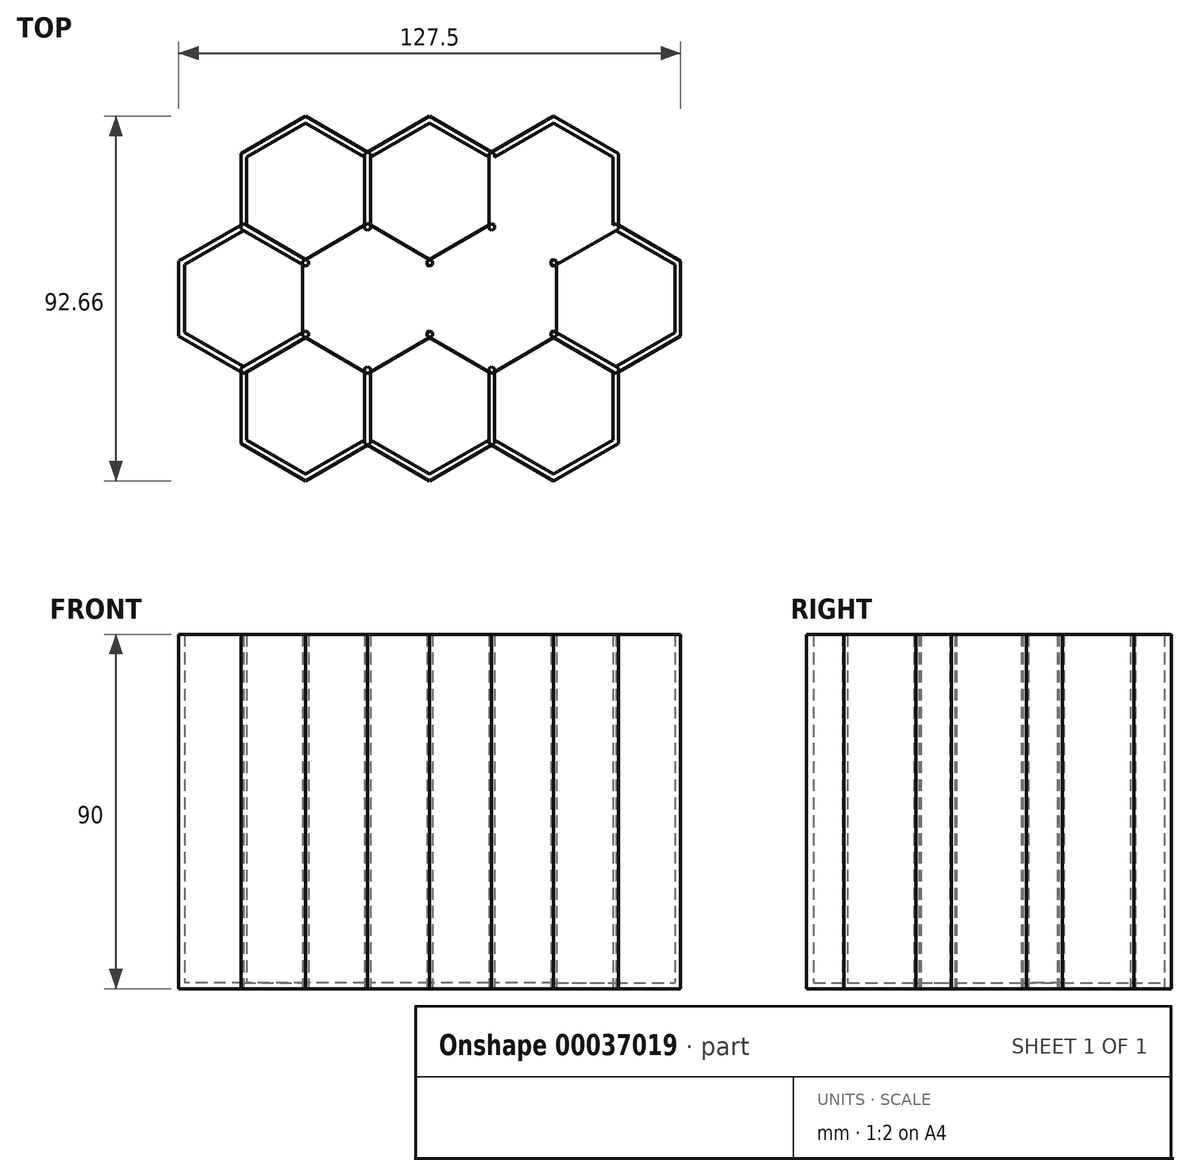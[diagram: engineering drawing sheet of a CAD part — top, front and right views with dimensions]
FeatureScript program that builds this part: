
annotation { "Feature Type Name" : "Feature", "Feature Type Description" : "" }
export const myFeature = defineFeature(function(context is Context, id is Id, definition is map)
    precondition{}
    {
        {
            assignVariable(context, id + "F0", {"name" : "WallThickness", "anyValue" : 1.5});
        }
        {
            var Q0;
            Q0=qCreatedBy(makeId("Top.planeOp"),FACE);
            var sketch = newSketch(context, id + "F1", { "sketchPlane" : qUnion([Q0])});
            skCircle(sketch, "E0.cCircle", {"center": v(0, 0) * mm, "radius": 15 * mm, "construction": true});
            skLineSegment(sketch, "E0.0", {"start": v(0, 17.32) * mm, "end": v(15, 8.66) * mm});
            skLineSegment(sketch, "E0.1", {"start": v(15, 8.66) * mm, "end": v(15, -8.66) * mm});
            skLineSegment(sketch, "E0.2", {"start": v(15, -8.66) * mm, "end": v(0, -17.32) * mm});
            skLineSegment(sketch, "E0.3", {"start": v(0, -17.32) * mm, "end": v(-15, -8.66) * mm});
            skLineSegment(sketch, "E0.4", {"start": v(-15, -8.66) * mm, "end": v(-15, 8.66) * mm});
            skLineSegment(sketch, "E0.5", {"start": v(-15, 8.66) * mm, "end": v(0, 17.32) * mm});
            skPoint(sketch, "E0.0.midPoint", {"position": v(7.5, 13) * mm});
            skLineSegment(sketch, "E1.0", {"start": v(-16.5, 9.53) * mm, "end": v(0, 19.05) * mm});
            skLineSegment(sketch, "E1.1", {"start": v(-16.5, -9.53) * mm, "end": v(-16.5, 9.53) * mm});
            skLineSegment(sketch, "E1.2", {"start": v(0, -19.05) * mm, "end": v(-16.5, -9.53) * mm});
            skLineSegment(sketch, "E1.3", {"start": v(16.5, -9.53) * mm, "end": v(0, -19.05) * mm});
            skLineSegment(sketch, "E1.4", {"start": v(16.5, 9.53) * mm, "end": v(16.5, -9.53) * mm});
            skLineSegment(sketch, "E1.5", {"start": v(0, 19.05) * mm, "end": v(16.5, 9.53) * mm});
            skCircle(sketch, "E2.1.0.0", {"center": v(31.5, 0) * mm, "radius": 15 * mm, "construction": true});
            skLineSegment(sketch, "E2.1.0.1", {"start": v(46.5, 8.66) * mm, "end": v(46.5, -8.66) * mm});
            skLineSegment(sketch, "E2.1.0.2", {"start": v(46.5, -8.66) * mm, "end": v(31.5, -17.32) * mm});
            skPoint(sketch, "E2.1.0.3", {"position": v(39, 13) * mm});
            skLineSegment(sketch, "E2.1.0.4", {"start": v(31.5, -19.05) * mm, "end": v(15, -9.53) * mm});
            skLineSegment(sketch, "E2.1.0.5", {"start": v(31.5, -17.32) * mm, "end": v(16.5, -8.66) * mm});
            skLineSegment(sketch, "E2.1.0.6", {"start": v(16.5, -8.66) * mm, "end": v(16.5, 8.66) * mm});
            skLineSegment(sketch, "E2.1.0.7", {"start": v(15, 9.53) * mm, "end": v(31.5, 19.05) * mm});
            skLineSegment(sketch, "E2.1.0.8", {"start": v(15, -9.53) * mm, "end": v(15, 9.53) * mm});
            skLineSegment(sketch, "E2.1.0.9", {"start": v(48, -9.53) * mm, "end": v(31.5, -19.05) * mm});
            skLineSegment(sketch, "E2.1.0.10", {"start": v(48, 9.53) * mm, "end": v(48, -9.53) * mm});
            skLineSegment(sketch, "E2.1.0.11", {"start": v(31.5, 19.05) * mm, "end": v(48, 9.53) * mm});
            skLineSegment(sketch, "E2.1.0.12", {"start": v(31.5, 17.32) * mm, "end": v(46.5, 8.66) * mm});
            skLineSegment(sketch, "E2.1.0.13", {"start": v(16.5, 8.66) * mm, "end": v(31.5, 17.32) * mm});
            skCircle(sketch, "E2.2.0.0", {"center": v(63, 0) * mm, "radius": 15 * mm, "construction": true});
            skLineSegment(sketch, "E2.2.0.1", {"start": v(78, 8.66) * mm, "end": v(78, -8.66) * mm});
            skLineSegment(sketch, "E2.2.0.2", {"start": v(78, -8.66) * mm, "end": v(63, -17.32) * mm});
            skPoint(sketch, "E2.2.0.3", {"position": v(70.5, 13) * mm});
            skLineSegment(sketch, "E2.2.0.4", {"start": v(63, -19.05) * mm, "end": v(46.5, -9.53) * mm});
            skLineSegment(sketch, "E2.2.0.5", {"start": v(63, -17.32) * mm, "end": v(48, -8.66) * mm});
            skLineSegment(sketch, "E2.2.0.6", {"start": v(48, -8.66) * mm, "end": v(48, 8.66) * mm});
            skLineSegment(sketch, "E2.2.0.7", {"start": v(46.5, 9.53) * mm, "end": v(63, 19.05) * mm});
            skLineSegment(sketch, "E2.2.0.8", {"start": v(46.5, -9.53) * mm, "end": v(46.5, 9.53) * mm});
            skLineSegment(sketch, "E2.2.0.9", {"start": v(79.5, -9.53) * mm, "end": v(63, -19.05) * mm});
            skLineSegment(sketch, "E2.2.0.10", {"start": v(79.5, 9.53) * mm, "end": v(79.5, -9.53) * mm});
            skLineSegment(sketch, "E2.2.0.11", {"start": v(63, 19.05) * mm, "end": v(79.5, 9.53) * mm});
            skLineSegment(sketch, "E2.2.0.12", {"start": v(63, 17.32) * mm, "end": v(78, 8.66) * mm});
            skLineSegment(sketch, "E2.2.0.13", {"start": v(48, 8.66) * mm, "end": v(63, 17.32) * mm});
            skLineSegment(sketch, "E2.direction1", {"start": v(0, 0) * mm, "end": v(31.5, 0) * mm, "construction": true});
            skLineSegment(sketch, "E3.1.0.0", {"start": v(-15.75, 46.33) * mm, "end": v(0.75, 36.8) * mm});
            skLineSegment(sketch, "E3.1.0.1", {"start": v(-15.75, 27.28) * mm, "end": v(15.75, 27.28) * mm, "construction": true});
            skLineSegment(sketch, "E3.1.0.2", {"start": v(-30.75, 18.62) * mm, "end": v(-30.75, 35.94) * mm});
            skLineSegment(sketch, "E3.1.0.3", {"start": v(-15.75, 9.96) * mm, "end": v(-30.75, 18.62) * mm});
            skLineSegment(sketch, "E3.1.0.4", {"start": v(-0.75, 18.62) * mm, "end": v(-15.75, 9.96) * mm});
            skLineSegment(sketch, "E3.1.0.5", {"start": v(-0.75, 35.94) * mm, "end": v(-0.75, 18.62) * mm});
            skLineSegment(sketch, "E3.1.0.6", {"start": v(0.75, 36.8) * mm, "end": v(0.75, 17.75) * mm});
            skPoint(sketch, "E3.1.0.7", {"position": v(-8.25, 40.27) * mm});
            skLineSegment(sketch, "E3.1.0.8", {"start": v(-15.75, 44.6) * mm, "end": v(-0.75, 35.94) * mm});
            skCircle(sketch, "E3.1.0.9", {"center": v(-15.75, 27.28) * mm, "radius": 15 * mm, "construction": true});
            skLineSegment(sketch, "E3.1.0.10", {"start": v(-32.25, 17.75) * mm, "end": v(-32.25, 36.8) * mm});
            skLineSegment(sketch, "E3.1.0.11", {"start": v(-15.75, 8.23) * mm, "end": v(-32.25, 17.75) * mm});
            skLineSegment(sketch, "E3.1.0.12", {"start": v(0.75, 17.75) * mm, "end": v(-15.75, 8.23) * mm});
            skLineSegment(sketch, "E3.1.0.13", {"start": v(-30.75, 35.94) * mm, "end": v(-15.75, 44.6) * mm});
            skLineSegment(sketch, "E3.1.0.14", {"start": v(-32.25, 36.8) * mm, "end": v(-15.75, 46.33) * mm});
            skLineSegment(sketch, "E3.direction1", {"start": v(0, 0) * mm, "end": v(-15.75, 27.28) * mm, "construction": true});
            skLineSegment(sketch, "E4.1.0.0", {"start": v(0.75, 35.94) * mm, "end": v(15.75, 44.6) * mm});
            skLineSegment(sketch, "E4.1.0.1", {"start": v(30.75, 35.94) * mm, "end": v(30.75, 18.62) * mm});
            skLineSegment(sketch, "E4.1.0.2", {"start": v(15.75, 8.23) * mm, "end": v(-0.75, 17.75) * mm});
            skLineSegment(sketch, "E4.1.0.3", {"start": v(0.75, 18.62) * mm, "end": v(0.75, 35.94) * mm});
            skLineSegment(sketch, "E4.1.0.4", {"start": v(32.25, 36.8) * mm, "end": v(32.25, 17.75) * mm});
            skLineSegment(sketch, "E4.1.0.5", {"start": v(-0.75, 36.8) * mm, "end": v(15.75, 46.33) * mm});
            skPoint(sketch, "E4.1.0.6", {"position": v(23.25, 40.27) * mm});
            skLineSegment(sketch, "E4.1.0.7", {"start": v(32.25, 17.75) * mm, "end": v(15.75, 8.23) * mm});
            skCircle(sketch, "E4.1.0.8", {"center": v(15.75, 27.28) * mm, "radius": 15 * mm, "construction": true});
            skLineSegment(sketch, "E4.1.0.9", {"start": v(-0.75, 17.75) * mm, "end": v(-0.75, 36.8) * mm});
            skLineSegment(sketch, "E4.1.0.10", {"start": v(30.75, 18.62) * mm, "end": v(15.75, 9.96) * mm});
            skLineSegment(sketch, "E4.1.0.11", {"start": v(15.75, 46.33) * mm, "end": v(32.25, 36.8) * mm});
            skLineSegment(sketch, "E4.1.0.12", {"start": v(15.75, 9.96) * mm, "end": v(0.75, 18.62) * mm});
            skLineSegment(sketch, "E4.1.0.13", {"start": v(15.75, 44.6) * mm, "end": v(30.75, 35.94) * mm});
            skLineSegment(sketch, "E4.2.0.0", {"start": v(32.25, 35.94) * mm, "end": v(47.25, 44.6) * mm});
            skLineSegment(sketch, "E4.2.0.1", {"start": v(62.25, 35.94) * mm, "end": v(62.25, 18.62) * mm});
            skLineSegment(sketch, "E4.2.0.2", {"start": v(47.25, 8.23) * mm, "end": v(30.75, 17.75) * mm});
            skLineSegment(sketch, "E4.2.0.3", {"start": v(32.25, 18.62) * mm, "end": v(32.25, 35.94) * mm});
            skLineSegment(sketch, "E4.2.0.4", {"start": v(63.75, 36.8) * mm, "end": v(63.75, 17.75) * mm});
            skLineSegment(sketch, "E4.2.0.5", {"start": v(30.75, 36.8) * mm, "end": v(47.25, 46.33) * mm});
            skPoint(sketch, "E4.2.0.6", {"position": v(54.75, 40.27) * mm});
            skLineSegment(sketch, "E4.2.0.7", {"start": v(63.75, 17.75) * mm, "end": v(47.25, 8.23) * mm});
            skCircle(sketch, "E4.2.0.8", {"center": v(47.25, 27.28) * mm, "radius": 15 * mm, "construction": true});
            skLineSegment(sketch, "E4.2.0.9", {"start": v(30.75, 17.75) * mm, "end": v(30.75, 36.8) * mm});
            skLineSegment(sketch, "E4.2.0.10", {"start": v(62.25, 18.62) * mm, "end": v(47.25, 9.96) * mm});
            skLineSegment(sketch, "E4.2.0.11", {"start": v(47.25, 46.33) * mm, "end": v(63.75, 36.8) * mm});
            skLineSegment(sketch, "E4.2.0.12", {"start": v(47.25, 9.96) * mm, "end": v(32.25, 18.62) * mm});
            skLineSegment(sketch, "E4.2.0.13", {"start": v(47.25, 44.6) * mm, "end": v(62.25, 35.94) * mm});
            skLineSegment(sketch, "E4.3.0.0", {"start": v(63.75, 35.94) * mm, "end": v(78.75, 44.6) * mm});
            skLineSegment(sketch, "E4.3.0.1", {"start": v(93.75, 35.94) * mm, "end": v(93.75, 18.62) * mm});
            skLineSegment(sketch, "E4.3.0.2", {"start": v(78.75, 8.23) * mm, "end": v(62.25, 17.75) * mm});
            skLineSegment(sketch, "E4.3.0.3", {"start": v(63.75, 18.62) * mm, "end": v(63.75, 35.94) * mm});
            skLineSegment(sketch, "E4.3.0.4", {"start": v(95.25, 36.8) * mm, "end": v(95.25, 17.75) * mm});
            skLineSegment(sketch, "E4.3.0.5", {"start": v(62.25, 36.8) * mm, "end": v(78.75, 46.33) * mm});
            skPoint(sketch, "E4.3.0.6", {"position": v(86.25, 40.27) * mm});
            skLineSegment(sketch, "E4.3.0.7", {"start": v(95.25, 17.75) * mm, "end": v(78.75, 8.23) * mm});
            skCircle(sketch, "E4.3.0.8", {"center": v(78.75, 27.28) * mm, "radius": 15 * mm, "construction": true});
            skLineSegment(sketch, "E4.3.0.9", {"start": v(62.25, 17.75) * mm, "end": v(62.25, 36.8) * mm});
            skLineSegment(sketch, "E4.3.0.10", {"start": v(93.75, 18.62) * mm, "end": v(78.75, 9.96) * mm});
            skLineSegment(sketch, "E4.3.0.11", {"start": v(78.75, 46.33) * mm, "end": v(95.25, 36.8) * mm});
            skLineSegment(sketch, "E4.3.0.12", {"start": v(78.75, 9.96) * mm, "end": v(63.75, 18.62) * mm});
            skLineSegment(sketch, "E4.3.0.13", {"start": v(78.75, 44.6) * mm, "end": v(93.75, 35.94) * mm});
            skLineSegment(sketch, "E5.1.0.0", {"start": v(-15, 45.9) * mm, "end": v(-15, 63.22) * mm});
            skLineSegment(sketch, "E5.1.0.1", {"start": v(78, 45.9) * mm, "end": v(63, 37.24) * mm});
            skLineSegment(sketch, "E5.1.0.2", {"start": v(0, 37.24) * mm, "end": v(-15, 45.9) * mm});
            skLineSegment(sketch, "E5.1.0.3", {"start": v(48, 64.09) * mm, "end": v(48, 45.03) * mm});
            skLineSegment(sketch, "E5.1.0.4", {"start": v(79.5, 45.03) * mm, "end": v(63, 35.5) * mm});
            skLineSegment(sketch, "E5.1.0.5", {"start": v(79.5, 64.09) * mm, "end": v(79.5, 45.03) * mm});
            skPoint(sketch, "E5.1.0.6", {"position": v(7.5, 67.55) * mm});
            skLineSegment(sketch, "E5.1.0.7", {"start": v(-15, 63.22) * mm, "end": v(0, 71.88) * mm});
            skLineSegment(sketch, "E5.1.0.8", {"start": v(0, 73.61) * mm, "end": v(16.5, 64.09) * mm});
            skLineSegment(sketch, "E5.1.0.9", {"start": v(15, 63.22) * mm, "end": v(15, 45.9) * mm});
            skLineSegment(sketch, "E5.1.0.10", {"start": v(48, 45.03) * mm, "end": v(31.5, 35.5) * mm});
            skLineSegment(sketch, "E5.1.0.11", {"start": v(48, 45.9) * mm, "end": v(48, 63.22) * mm});
            skLineSegment(sketch, "E5.1.0.12", {"start": v(46.5, 63.22) * mm, "end": v(46.5, 45.9) * mm});
            skCircle(sketch, "E5.1.0.13", {"center": v(63, 54.56) * mm, "radius": 15 * mm, "construction": true});
            skLineSegment(sketch, "E5.1.0.14", {"start": v(16.5, 63.22) * mm, "end": v(31.5, 71.88) * mm});
            skLineSegment(sketch, "E5.1.0.15", {"start": v(0, 71.88) * mm, "end": v(15, 63.22) * mm});
            skPoint(sketch, "E5.1.0.16", {"position": v(39, 67.55) * mm});
            skLineSegment(sketch, "E5.1.0.17", {"start": v(63, 35.5) * mm, "end": v(46.5, 45.03) * mm});
            skLineSegment(sketch, "E5.1.0.18", {"start": v(63, 37.24) * mm, "end": v(48, 45.9) * mm});
            skLineSegment(sketch, "E5.1.0.19", {"start": v(15, 45.03) * mm, "end": v(15, 64.09) * mm});
            skLineSegment(sketch, "E5.1.0.20", {"start": v(15, 64.09) * mm, "end": v(31.5, 73.61) * mm});
            skLineSegment(sketch, "E5.1.0.21", {"start": v(31.5, 73.61) * mm, "end": v(48, 64.09) * mm});
            skLineSegment(sketch, "E5.1.0.22", {"start": v(-16.5, 45.03) * mm, "end": v(-16.5, 64.09) * mm});
            skLineSegment(sketch, "E5.1.0.23", {"start": v(46.5, 45.03) * mm, "end": v(46.5, 64.09) * mm});
            skLineSegment(sketch, "E5.1.0.24", {"start": v(63, 73.61) * mm, "end": v(79.5, 64.09) * mm});
            skLineSegment(sketch, "E5.1.0.25", {"start": v(48, 63.22) * mm, "end": v(63, 71.88) * mm});
            skLineSegment(sketch, "E5.1.0.26", {"start": v(31.5, 35.5) * mm, "end": v(15, 45.03) * mm});
            skCircle(sketch, "E5.1.0.27", {"center": v(0, 54.56) * mm, "radius": 15 * mm, "construction": true});
            skLineSegment(sketch, "E5.1.0.28", {"start": v(0, 54.56) * mm, "end": v(31.5, 54.56) * mm, "construction": true});
            skLineSegment(sketch, "E5.1.0.29", {"start": v(46.5, 64.09) * mm, "end": v(63, 73.61) * mm});
            skLineSegment(sketch, "E5.1.0.30", {"start": v(31.5, 37.24) * mm, "end": v(16.5, 45.9) * mm});
            skLineSegment(sketch, "E5.1.0.31", {"start": v(0, 35.5) * mm, "end": v(-16.5, 45.03) * mm});
            skLineSegment(sketch, "E5.1.0.32", {"start": v(15, 45.9) * mm, "end": v(0, 37.24) * mm});
            skCircle(sketch, "E5.1.0.33", {"center": v(31.5, 54.56) * mm, "radius": 15 * mm, "construction": true});
            skLineSegment(sketch, "E5.1.0.34", {"start": v(78, 63.22) * mm, "end": v(78, 45.9) * mm});
            skLineSegment(sketch, "E5.1.0.35", {"start": v(16.5, 64.09) * mm, "end": v(16.5, 45.03) * mm});
            skLineSegment(sketch, "E5.1.0.36", {"start": v(16.5, 45.03) * mm, "end": v(0, 35.5) * mm});
            skLineSegment(sketch, "E5.1.0.37", {"start": v(-16.5, 64.09) * mm, "end": v(0, 73.61) * mm});
            skLineSegment(sketch, "E5.1.0.38", {"start": v(16.5, 45.9) * mm, "end": v(16.5, 63.22) * mm});
            skLineSegment(sketch, "E5.1.0.39", {"start": v(46.5, 45.9) * mm, "end": v(31.5, 37.24) * mm});
            skLineSegment(sketch, "E5.1.0.40", {"start": v(0, 54.56) * mm, "end": v(31.5, 54.56) * mm, "construction": true});
            skPoint(sketch, "E5.1.0.41", {"position": v(70.5, 67.55) * mm});
            skLineSegment(sketch, "E5.1.0.42", {"start": v(31.5, 71.88) * mm, "end": v(46.5, 63.22) * mm});
            skLineSegment(sketch, "E5.1.0.43", {"start": v(63, 71.88) * mm, "end": v(78, 63.22) * mm});
            skLineSegment(sketch, "E5.direction1", {"start": v(-15.75, 27.28) * mm, "end": v(0, 54.56) * mm, "construction": true});
            skSolve(sketch);
        }
        {
            assignVariable(context, id + "F2", {"name" : "Height", "anyValue" : 90});
        }
        {
            var Q0;
            {var subQ2=sQuery(id+"F1.wireOp",EDGE,"E5.1.0.14");Q0=makeQuery(id+"F1.imprint","IMPRINT",FACE,{"disambiguationData":[TD([[makeQuery(id+"F1.imprint","IMPRINT",EDGE,{"derivedFrom":subQ2}),1.0]])]});}
            var Q1;
            {var subQ10=sQuery(id+"F1.wireOp",EDGE,"E5.1.0.0");Q1=makeQuery(id+"F1.imprint","IMPRINT",FACE,{"disambiguationData":[TD([[makeQuery(id+"F1.imprint","IMPRINT",EDGE,{"derivedFrom":subQ10}),1.0]])]});}
            var Q2;
            Q2=makeQuery(id+"F1.imprint","IMPRINT",FACE,{"disambiguationData":[TD([[makeQuery(id+"F1.imprint","IMPRINT",EDGE,{"derivedFrom":sQuery(id+"F1.wireOp",EDGE,"E4.3.0.1")}),1.0]])]});
            var Q3;
            {var subQ5=sQuery(id+"F1.wireOp",EDGE,"E2.2.0.1");Q3=makeQuery(id+"F1.imprint","IMPRINT",FACE,{"disambiguationData":[TD([[makeQuery(id+"F1.imprint","IMPRINT",EDGE,{"derivedFrom":subQ5}),1.0]])]});}
            var Q4;
            {var subQ3=sQuery(id+"F1.wireOp",EDGE,"E2.1.0.2");Q4=makeQuery(id+"F1.imprint","IMPRINT",FACE,{"disambiguationData":[TD([[makeQuery(id+"F1.imprint","IMPRINT",EDGE,{"derivedFrom":subQ3}),1.0]])]});}
            var Q5;
            Q5=makeQuery(id+"F1.imprint","IMPRINT",FACE,{"disambiguationData":[TD([[makeQuery(id+"F1.imprint","IMPRINT",EDGE,{"derivedFrom":sQuery(id+"F1.wireOp",EDGE,"E3.1.0.2")}),1.0]])]});
            var Q6;
            {var subQ9=sQuery(id+"F1.wireOp",EDGE,"E0.2");Q6=makeQuery(id+"F1.imprint","IMPRINT",FACE,{"disambiguationData":[TD([[makeQuery(id+"F1.imprint","IMPRINT",EDGE,{"derivedFrom":subQ9}),1.0]])]});}
            var Q7;
            {var subQ4=sQuery(id+"F1.wireOp",EDGE,"E2.1.0.6");Q7=makeQuery(id+"F1.imprint","IMPRINT",FACE,{"disambiguationData":[TD([[makeQuery(id+"F1.imprint","IMPRINT",EDGE,{"derivedFrom":subQ4}),1.0]])]});}
            var Q8;
            {var subQ4=sQuery(id+"F1.wireOp",EDGE,"E5.1.0.24");Q8=makeQuery(id+"F1.imprint","IMPRINT",FACE,{"disambiguationData":[TD([[makeQuery(id+"F1.imprint","IMPRINT",EDGE,{"derivedFrom":subQ4}),-1.0]])]});}
            var Q9;
            {var subQ0=sQuery(id+"F1.wireOp",EDGE,"E4.2.0.12");Q9=makeQuery(id+"F1.imprint","IMPRINT",FACE,{"disambiguationData":[TD([[makeQuery(id+"F1.imprint","IMPRINT",EDGE,{"derivedFrom":subQ0}),1.0]])]});}
            var Q10;
            {var subQ0=sQuery(id+"F1.wireOp",EDGE,"E5.1.0.38");Q10=makeQuery(id+"F1.imprint","IMPRINT",FACE,{"disambiguationData":[TD([[makeQuery(id+"F1.imprint","IMPRINT",EDGE,{"derivedFrom":subQ0}),1.0]])]});}
            var Q11;
            {var subQ8=sQuery(id+"F1.wireOp",EDGE,"E5.1.0.2");Q11=makeQuery(id+"F1.imprint","IMPRINT",FACE,{"disambiguationData":[TD([[makeQuery(id+"F1.imprint","IMPRINT",EDGE,{"derivedFrom":subQ8}),1.0]])]});}
            var Q12;
            {var subQ4=sQuery(id+"F1.wireOp",EDGE,"E4.2.0.10");Q12=makeQuery(id+"F1.imprint","IMPRINT",FACE,{"disambiguationData":[TD([[makeQuery(id+"F1.imprint","IMPRINT",EDGE,{"derivedFrom":subQ4}),1.0]])]});}
            var Q13;
            {var subQ0=sQuery(id+"F1.wireOp",EDGE,"E4.3.0.12");Q13=makeQuery(id+"F1.imprint","IMPRINT",FACE,{"disambiguationData":[TD([[makeQuery(id+"F1.imprint","IMPRINT",EDGE,{"derivedFrom":subQ0}),1.0]])]});}
            var Q14;
            {var subQ6=sQuery(id+"F1.wireOp",EDGE,"E4.2.0.3");Q14=makeQuery(id+"F1.imprint","IMPRINT",FACE,{"disambiguationData":[TD([[makeQuery(id+"F1.imprint","IMPRINT",EDGE,{"derivedFrom":subQ6}),1.0]])]});}
            var Q15;
            {var subQ8=sQuery(id+"F1.wireOp",EDGE,"E2.2.0.6");Q15=makeQuery(id+"F1.imprint","IMPRINT",FACE,{"disambiguationData":[TD([[makeQuery(id+"F1.imprint","IMPRINT",EDGE,{"derivedFrom":subQ8}),1.0]])]});}
            var Q16;
            {var subQ0=sQuery(id+"F1.wireOp",EDGE,"E4.1.0.12");Q16=makeQuery(id+"F1.imprint","IMPRINT",FACE,{"disambiguationData":[TD([[makeQuery(id+"F1.imprint","IMPRINT",EDGE,{"derivedFrom":subQ0}),1.0]])]});}
            var Q17;
            {var subQ4=sQuery(id+"F1.wireOp",EDGE,"E4.1.0.10");Q17=makeQuery(id+"F1.imprint","IMPRINT",FACE,{"disambiguationData":[TD([[makeQuery(id+"F1.imprint","IMPRINT",EDGE,{"derivedFrom":subQ4}),1.0]])]});}
            var Q18;
            {var subQ4=sQuery(id+"F1.wireOp",EDGE,"E3.1.0.4");Q18=makeQuery(id+"F1.imprint","IMPRINT",FACE,{"disambiguationData":[TD([[makeQuery(id+"F1.imprint","IMPRINT",EDGE,{"derivedFrom":subQ4}),1.0]])]});}
            var Q19;
            {var subQ4=sQuery(id+"F1.wireOp",EDGE,"E4.1.0.3");Q19=makeQuery(id+"F1.imprint","IMPRINT",FACE,{"disambiguationData":[TD([[makeQuery(id+"F1.imprint","IMPRINT",EDGE,{"derivedFrom":subQ4}),1.0]])]});}
            var Q20;
            {var subQ0=sQuery(id+"F1.wireOp",EDGE,"E5.1.0.18");Q20=makeQuery(id+"F1.imprint","IMPRINT",FACE,{"disambiguationData":[TD([[makeQuery(id+"F1.imprint","IMPRINT",EDGE,{"derivedFrom":subQ0}),1.0]])]});}
            var Q21;
            {var subQ6=sQuery(id+"F1.wireOp",EDGE,"E5.1.0.30");Q21=makeQuery(id+"F1.imprint","IMPRINT",FACE,{"disambiguationData":[TD([[makeQuery(id+"F1.imprint","IMPRINT",EDGE,{"derivedFrom":subQ6}),1.0]])]});}
            var Q22;
            {var subQ5=sQuery(id+"F1.wireOp",EDGE,"E5.1.0.32");Q22=makeQuery(id+"F1.imprint","IMPRINT",FACE,{"disambiguationData":[TD([[makeQuery(id+"F1.imprint","IMPRINT",EDGE,{"derivedFrom":subQ5}),1.0]])]});}
            var Q23;
            {var subQ10=sQuery(id+"F1.wireOp",EDGE,"E5.1.0.11");Q23=makeQuery(id+"F1.imprint","IMPRINT",FACE,{"disambiguationData":[TD([[makeQuery(id+"F1.imprint","IMPRINT",EDGE,{"derivedFrom":subQ10}),1.0]])]});}
            var Q24;
            {var subQ0=sQuery(id+"F1.wireOp",EDGE,"E5.1.0.39");Q24=makeQuery(id+"F1.imprint","IMPRINT",FACE,{"disambiguationData":[TD([[makeQuery(id+"F1.imprint","IMPRINT",EDGE,{"derivedFrom":subQ0}),1.0]])]});}
            var Q25;
            {var subQ6=sQuery(id+"F1.wireOp",EDGE,"E4.3.0.3");Q25=makeQuery(id+"F1.imprint","IMPRINT",FACE,{"disambiguationData":[TD([[makeQuery(id+"F1.imprint","IMPRINT",EDGE,{"derivedFrom":subQ6}),1.0]])]});}
            var Q26;
            {var subQ8=sQuery(id+"F1.wireOp",EDGE,"E5.1.0.1");Q26=makeQuery(id+"F1.imprint","IMPRINT",FACE,{"disambiguationData":[TD([[makeQuery(id+"F1.imprint","IMPRINT",EDGE,{"derivedFrom":subQ8}),1.0]])]});}
            var Q27;
            {var subQ1=sQuery(id+"F1.wireOp",EDGE,"E4.2.0.9");var subQ7=sQuery(id+"F1.wireOp",EDGE,"E4.2.0.5");var subQ8=makeQuery(id+"F1.imprint","INTERSECT",VERTEX,{"derivedFrom":[subQ7,subQ1]});Q27=makeQuery(id+"F1.imprint","IMPRINT",FACE,{"disambiguationData":[TD([[makeQuery(id+"F1.imprint","IMPRINT",EDGE,{"disambiguationData":[TD([[subQ8,1.0]])],"derivedFrom":subQ1}),-1.0]])]});}
            var Q28;
            {var subQ1=sQuery(id+"F1.wireOp",EDGE,"E2.1.0.8");var subQ5=sQuery(id+"F1.wireOp",EDGE,"E2.1.0.7");var subQ6=makeQuery(id+"F1.imprint","INTERSECT",VERTEX,{"derivedFrom":[subQ5,subQ1]});Q28=makeQuery(id+"F1.imprint","IMPRINT",FACE,{"disambiguationData":[TD([[makeQuery(id+"F1.imprint","IMPRINT",EDGE,{"disambiguationData":[TD([[subQ6,1.0]])],"derivedFrom":subQ1}),-1.0]])]});}
            var Q29;
            {var subQ5=sQuery(id+"F1.wireOp",EDGE,"E5.1.0.10");var subQ7=sQuery(id+"F1.wireOp",EDGE,"E5.1.0.3");var subQ8=makeQuery(id+"F1.imprint","INTERSECT",VERTEX,{"derivedFrom":[subQ7,subQ5]});Q29=makeQuery(id+"F1.imprint","IMPRINT",FACE,{"disambiguationData":[TD([[makeQuery(id+"F1.imprint","IMPRINT",EDGE,{"disambiguationData":[TD([[subQ8,-1.0]])],"derivedFrom":subQ5}),-1.0]])]});}
            var Q30;
            {var subQ5=sQuery(id+"F1.wireOp",EDGE,"E4.1.0.9");var subQ7=sQuery(id+"F1.wireOp",EDGE,"E4.1.0.5");var subQ8=makeQuery(id+"F1.imprint","INTERSECT",VERTEX,{"derivedFrom":[subQ7,subQ5]});Q30=makeQuery(id+"F1.imprint","IMPRINT",FACE,{"disambiguationData":[TD([[makeQuery(id+"F1.imprint","IMPRINT",EDGE,{"disambiguationData":[TD([[subQ8,1.0]])],"derivedFrom":subQ5}),-1.0]])]});}
            var Q31;
            {var subQ5=sQuery(id+"F1.wireOp",EDGE,"E4.2.0.7");var subQ7=sQuery(id+"F1.wireOp",EDGE,"E4.2.0.4");var subQ8=makeQuery(id+"F1.imprint","INTERSECT",VERTEX,{"derivedFrom":[subQ7,subQ5]});Q31=makeQuery(id+"F1.imprint","IMPRINT",FACE,{"disambiguationData":[TD([[makeQuery(id+"F1.imprint","IMPRINT",EDGE,{"disambiguationData":[TD([[subQ8,-1.0]])],"derivedFrom":subQ5}),-1.0]])]});}
            var Q32;
            {var subQ5=sQuery(id+"F1.wireOp",EDGE,"E3.1.0.12");var subQ7=sQuery(id+"F1.wireOp",EDGE,"E3.1.0.6");var subQ8=makeQuery(id+"F1.imprint","INTERSECT",VERTEX,{"derivedFrom":[subQ7,subQ5]});Q32=makeQuery(id+"F1.imprint","IMPRINT",FACE,{"disambiguationData":[TD([[makeQuery(id+"F1.imprint","IMPRINT",EDGE,{"disambiguationData":[TD([[subQ8,-1.0]])],"derivedFrom":subQ5}),-1.0]])]});}
            var Q33;
            {var subQ1=sQuery(id+"F1.wireOp",EDGE,"E4.3.0.9");var subQ7=sQuery(id+"F1.wireOp",EDGE,"E4.3.0.5");var subQ8=makeQuery(id+"F1.imprint","INTERSECT",VERTEX,{"derivedFrom":[subQ7,subQ1]});Q33=makeQuery(id+"F1.imprint","IMPRINT",FACE,{"disambiguationData":[TD([[makeQuery(id+"F1.imprint","IMPRINT",EDGE,{"disambiguationData":[TD([[subQ8,1.0]])],"derivedFrom":subQ1}),-1.0]])]});}
            var Q34;
            {var subQ1=sQuery(id+"F1.wireOp",EDGE,"E5.1.0.26");var subQ7=sQuery(id+"F1.wireOp",EDGE,"E5.1.0.19");var subQ8=makeQuery(id+"F1.imprint","INTERSECT",VERTEX,{"derivedFrom":[subQ7,subQ1]});Q34=makeQuery(id+"F1.imprint","IMPRINT",FACE,{"disambiguationData":[TD([[makeQuery(id+"F1.imprint","IMPRINT",EDGE,{"disambiguationData":[TD([[subQ8,1.0]])],"derivedFrom":subQ1}),-1.0]])]});}
            var Q35;
            {var subQ5=sQuery(id+"F1.wireOp",EDGE,"E2.2.0.8");var subQ7=sQuery(id+"F1.wireOp",EDGE,"E2.2.0.7");var subQ8=makeQuery(id+"F1.imprint","INTERSECT",VERTEX,{"derivedFrom":[subQ7,subQ5]});Q35=makeQuery(id+"F1.imprint","IMPRINT",FACE,{"disambiguationData":[TD([[makeQuery(id+"F1.imprint","IMPRINT",EDGE,{"disambiguationData":[TD([[subQ8,1.0]])],"derivedFrom":subQ5}),-1.0]])]});}
            var Q36;
            {var subQ5=sQuery(id+"F1.wireOp",EDGE,"E4.1.0.7");var subQ7=sQuery(id+"F1.wireOp",EDGE,"E4.1.0.4");var subQ8=makeQuery(id+"F1.imprint","INTERSECT",VERTEX,{"derivedFrom":[subQ7,subQ5]});Q36=makeQuery(id+"F1.imprint","IMPRINT",FACE,{"disambiguationData":[TD([[makeQuery(id+"F1.imprint","IMPRINT",EDGE,{"disambiguationData":[TD([[subQ8,-1.0]])],"derivedFrom":subQ5}),-1.0]])]});}
            extrude(context, id + "F3", {"entities" : qUnion([Q0, Q1, Q2, Q3, Q4, Q5, Q6, Q7, Q8, Q9, Q10, Q11, Q12, Q13, Q14, Q15, Q16, Q17, Q18, Q19, Q20, Q21, Q22, Q23, Q24, Q25, Q26, Q27, Q28, Q29, Q30, Q31, Q32, Q33, Q34, Q35, Q36]), "depth" : (getVariable(context, 'Height')) * mm});
        }
        {
            var Q0;
            {var subQ3=sQuery(id+"F1.wireOp",EDGE,"E4.1.0.3");Q0=makeQuery(id+"F1.imprint","IMPRINT",FACE,{"disambiguationData":[TD([[makeQuery(id+"F1.imprint","IMPRINT",EDGE,{"derivedFrom":subQ3}),-1.0]])]});}
            var Q1;
            {var subQ5=sQuery(id+"F1.wireOp",EDGE,"E4.2.0.3");Q1=makeQuery(id+"F1.imprint","IMPRINT",FACE,{"disambiguationData":[TD([[makeQuery(id+"F1.imprint","IMPRINT",EDGE,{"derivedFrom":subQ5}),-1.0]])]});}
            var Q2;
            Q2=makeQuery(id+"F1.imprint","IMPRINT",FACE,{"disambiguationData":[TD([[makeQuery(id+"F1.imprint","IMPRINT",EDGE,{"derivedFrom":sQuery(id+"F1.wireOp",EDGE,"E5.1.0.14")}),-1.0]])]});
            var Q3;
            Q3=makeQuery(id+"F1.imprint","IMPRINT",FACE,{"disambiguationData":[TD([[makeQuery(id+"F1.imprint","IMPRINT",EDGE,{"derivedFrom":sQuery(id+"F1.wireOp",EDGE,"E3.1.0.2")}),-1.0]])]});
            var Q4;
            Q4=makeQuery(id+"F1.imprint","IMPRINT",FACE,{"disambiguationData":[TD([[makeQuery(id+"F1.imprint","IMPRINT",EDGE,{"derivedFrom":sQuery(id+"F1.wireOp",EDGE,"E5.1.0.0")}),-1.0]])]});
            var Q5;
            {var subQ6=sQuery(id+"F1.wireOp",EDGE,"E0.2");Q5=makeQuery(id+"F1.imprint","IMPRINT",FACE,{"disambiguationData":[TD([[makeQuery(id+"F1.imprint","IMPRINT",EDGE,{"derivedFrom":subQ6}),-1.0]])]});}
            var Q6;
            Q6=makeQuery(id+"F1.imprint","IMPRINT",FACE,{"disambiguationData":[TD([[makeQuery(id+"F1.imprint","IMPRINT",EDGE,{"derivedFrom":sQuery(id+"F1.wireOp",EDGE,"E5.1.0.1")}),-1.0]])]});
            var Q7;
            {var subQ6=sQuery(id+"F1.wireOp",EDGE,"E2.1.0.2");Q7=makeQuery(id+"F1.imprint","IMPRINT",FACE,{"disambiguationData":[TD([[makeQuery(id+"F1.imprint","IMPRINT",EDGE,{"derivedFrom":subQ6}),-1.0]])]});}
            var Q8;
            {var subQ3=sQuery(id+"F1.wireOp",EDGE,"E2.2.0.1");Q8=makeQuery(id+"F1.imprint","IMPRINT",FACE,{"disambiguationData":[TD([[makeQuery(id+"F1.imprint","IMPRINT",EDGE,{"derivedFrom":subQ3}),-1.0]])]});}
            var Q9;
            Q9=makeQuery(id+"F1.imprint","IMPRINT",FACE,{"disambiguationData":[TD([[makeQuery(id+"F1.imprint","IMPRINT",EDGE,{"derivedFrom":sQuery(id+"F1.wireOp",EDGE,"E4.3.0.1")}),-1.0]])]});
            var Q10;
            {var subQ4=sQuery(id+"F1.wireOp",EDGE,"E5.1.0.24");Q10=makeQuery(id+"F1.imprint","IMPRINT",FACE,{"disambiguationData":[TD([[makeQuery(id+"F1.imprint","IMPRINT",EDGE,{"derivedFrom":subQ4}),-1.0]])]});}
            var Q11;
            {var subQ2=sQuery(id+"F1.wireOp",EDGE,"E5.1.0.14");Q11=makeQuery(id+"F1.imprint","IMPRINT",FACE,{"disambiguationData":[TD([[makeQuery(id+"F1.imprint","IMPRINT",EDGE,{"derivedFrom":subQ2}),1.0]])]});}
            var Q12;
            {var subQ9=sQuery(id+"F1.wireOp",EDGE,"E0.2");Q12=makeQuery(id+"F1.imprint","IMPRINT",FACE,{"disambiguationData":[TD([[makeQuery(id+"F1.imprint","IMPRINT",EDGE,{"derivedFrom":subQ9}),1.0]])]});}
            var Q13;
            Q13=makeQuery(id+"F1.imprint","IMPRINT",FACE,{"disambiguationData":[TD([[makeQuery(id+"F1.imprint","IMPRINT",EDGE,{"derivedFrom":sQuery(id+"F1.wireOp",EDGE,"E3.1.0.2")}),1.0]])]});
            var Q14;
            {var subQ3=sQuery(id+"F1.wireOp",EDGE,"E2.1.0.2");Q14=makeQuery(id+"F1.imprint","IMPRINT",FACE,{"disambiguationData":[TD([[makeQuery(id+"F1.imprint","IMPRINT",EDGE,{"derivedFrom":subQ3}),1.0]])]});}
            var Q15;
            {var subQ5=sQuery(id+"F1.wireOp",EDGE,"E2.2.0.1");Q15=makeQuery(id+"F1.imprint","IMPRINT",FACE,{"disambiguationData":[TD([[makeQuery(id+"F1.imprint","IMPRINT",EDGE,{"derivedFrom":subQ5}),1.0]])]});}
            var Q16;
            Q16=makeQuery(id+"F1.imprint","IMPRINT",FACE,{"disambiguationData":[TD([[makeQuery(id+"F1.imprint","IMPRINT",EDGE,{"derivedFrom":sQuery(id+"F1.wireOp",EDGE,"E4.3.0.1")}),1.0]])]});
            var Q17;
            {var subQ10=sQuery(id+"F1.wireOp",EDGE,"E5.1.0.0");Q17=makeQuery(id+"F1.imprint","IMPRINT",FACE,{"disambiguationData":[TD([[makeQuery(id+"F1.imprint","IMPRINT",EDGE,{"derivedFrom":subQ10}),1.0]])]});}
            var Q18;
            {var subQ8=sQuery(id+"F1.wireOp",EDGE,"E5.1.0.1");Q18=makeQuery(id+"F1.imprint","IMPRINT",FACE,{"disambiguationData":[TD([[makeQuery(id+"F1.imprint","IMPRINT",EDGE,{"derivedFrom":subQ8}),1.0]])]});}
            var Q19;
            {var subQ6=sQuery(id+"F1.wireOp",EDGE,"E4.3.0.3");Q19=makeQuery(id+"F1.imprint","IMPRINT",FACE,{"disambiguationData":[TD([[makeQuery(id+"F1.imprint","IMPRINT",EDGE,{"derivedFrom":subQ6}),1.0]])]});}
            var Q20;
            {var subQ0=sQuery(id+"F1.wireOp",EDGE,"E5.1.0.39");Q20=makeQuery(id+"F1.imprint","IMPRINT",FACE,{"disambiguationData":[TD([[makeQuery(id+"F1.imprint","IMPRINT",EDGE,{"derivedFrom":subQ0}),1.0]])]});}
            var Q21;
            {var subQ10=sQuery(id+"F1.wireOp",EDGE,"E5.1.0.11");Q21=makeQuery(id+"F1.imprint","IMPRINT",FACE,{"disambiguationData":[TD([[makeQuery(id+"F1.imprint","IMPRINT",EDGE,{"derivedFrom":subQ10}),1.0]])]});}
            var Q22;
            {var subQ5=sQuery(id+"F1.wireOp",EDGE,"E5.1.0.32");Q22=makeQuery(id+"F1.imprint","IMPRINT",FACE,{"disambiguationData":[TD([[makeQuery(id+"F1.imprint","IMPRINT",EDGE,{"derivedFrom":subQ5}),1.0]])]});}
            var Q23;
            {var subQ6=sQuery(id+"F1.wireOp",EDGE,"E5.1.0.30");Q23=makeQuery(id+"F1.imprint","IMPRINT",FACE,{"disambiguationData":[TD([[makeQuery(id+"F1.imprint","IMPRINT",EDGE,{"derivedFrom":subQ6}),1.0]])]});}
            var Q24;
            {var subQ0=sQuery(id+"F1.wireOp",EDGE,"E5.1.0.18");Q24=makeQuery(id+"F1.imprint","IMPRINT",FACE,{"disambiguationData":[TD([[makeQuery(id+"F1.imprint","IMPRINT",EDGE,{"derivedFrom":subQ0}),1.0]])]});}
            var Q25;
            {var subQ4=sQuery(id+"F1.wireOp",EDGE,"E4.1.0.3");Q25=makeQuery(id+"F1.imprint","IMPRINT",FACE,{"disambiguationData":[TD([[makeQuery(id+"F1.imprint","IMPRINT",EDGE,{"derivedFrom":subQ4}),1.0]])]});}
            var Q26;
            {var subQ4=sQuery(id+"F1.wireOp",EDGE,"E3.1.0.4");Q26=makeQuery(id+"F1.imprint","IMPRINT",FACE,{"disambiguationData":[TD([[makeQuery(id+"F1.imprint","IMPRINT",EDGE,{"derivedFrom":subQ4}),1.0]])]});}
            var Q27;
            {var subQ4=sQuery(id+"F1.wireOp",EDGE,"E4.1.0.10");Q27=makeQuery(id+"F1.imprint","IMPRINT",FACE,{"disambiguationData":[TD([[makeQuery(id+"F1.imprint","IMPRINT",EDGE,{"derivedFrom":subQ4}),1.0]])]});}
            var Q28;
            {var subQ4=sQuery(id+"F1.wireOp",EDGE,"E2.1.0.6");Q28=makeQuery(id+"F1.imprint","IMPRINT",FACE,{"disambiguationData":[TD([[makeQuery(id+"F1.imprint","IMPRINT",EDGE,{"derivedFrom":subQ4}),1.0]])]});}
            var Q29;
            {var subQ0=sQuery(id+"F1.wireOp",EDGE,"E4.1.0.12");Q29=makeQuery(id+"F1.imprint","IMPRINT",FACE,{"disambiguationData":[TD([[makeQuery(id+"F1.imprint","IMPRINT",EDGE,{"derivedFrom":subQ0}),1.0]])]});}
            var Q30;
            {var subQ8=sQuery(id+"F1.wireOp",EDGE,"E2.2.0.6");Q30=makeQuery(id+"F1.imprint","IMPRINT",FACE,{"disambiguationData":[TD([[makeQuery(id+"F1.imprint","IMPRINT",EDGE,{"derivedFrom":subQ8}),1.0]])]});}
            var Q31;
            {var subQ6=sQuery(id+"F1.wireOp",EDGE,"E4.2.0.3");Q31=makeQuery(id+"F1.imprint","IMPRINT",FACE,{"disambiguationData":[TD([[makeQuery(id+"F1.imprint","IMPRINT",EDGE,{"derivedFrom":subQ6}),1.0]])]});}
            var Q32;
            {var subQ0=sQuery(id+"F1.wireOp",EDGE,"E4.3.0.12");Q32=makeQuery(id+"F1.imprint","IMPRINT",FACE,{"disambiguationData":[TD([[makeQuery(id+"F1.imprint","IMPRINT",EDGE,{"derivedFrom":subQ0}),1.0]])]});}
            var Q33;
            {var subQ4=sQuery(id+"F1.wireOp",EDGE,"E4.2.0.10");Q33=makeQuery(id+"F1.imprint","IMPRINT",FACE,{"disambiguationData":[TD([[makeQuery(id+"F1.imprint","IMPRINT",EDGE,{"derivedFrom":subQ4}),1.0]])]});}
            var Q34;
            {var subQ8=sQuery(id+"F1.wireOp",EDGE,"E5.1.0.2");Q34=makeQuery(id+"F1.imprint","IMPRINT",FACE,{"disambiguationData":[TD([[makeQuery(id+"F1.imprint","IMPRINT",EDGE,{"derivedFrom":subQ8}),1.0]])]});}
            var Q35;
            {var subQ0=sQuery(id+"F1.wireOp",EDGE,"E5.1.0.38");Q35=makeQuery(id+"F1.imprint","IMPRINT",FACE,{"disambiguationData":[TD([[makeQuery(id+"F1.imprint","IMPRINT",EDGE,{"derivedFrom":subQ0}),1.0]])]});}
            var Q36;
            {var subQ0=sQuery(id+"F1.wireOp",EDGE,"E4.2.0.12");Q36=makeQuery(id+"F1.imprint","IMPRINT",FACE,{"disambiguationData":[TD([[makeQuery(id+"F1.imprint","IMPRINT",EDGE,{"derivedFrom":subQ0}),1.0]])]});}
            var Q37;
            {var subQ5=sQuery(id+"F1.wireOp",EDGE,"E5.1.0.10");var subQ7=sQuery(id+"F1.wireOp",EDGE,"E5.1.0.3");var subQ8=makeQuery(id+"F1.imprint","INTERSECT",VERTEX,{"derivedFrom":[subQ7,subQ5]});Q37=makeQuery(id+"F1.imprint","IMPRINT",FACE,{"disambiguationData":[TD([[makeQuery(id+"F1.imprint","IMPRINT",EDGE,{"disambiguationData":[TD([[subQ8,-1.0]])],"derivedFrom":subQ5}),-1.0]])]});}
            var Q38;
            {var subQ1=sQuery(id+"F1.wireOp",EDGE,"E5.1.0.26");var subQ7=sQuery(id+"F1.wireOp",EDGE,"E5.1.0.19");var subQ8=makeQuery(id+"F1.imprint","INTERSECT",VERTEX,{"derivedFrom":[subQ7,subQ1]});Q38=makeQuery(id+"F1.imprint","IMPRINT",FACE,{"disambiguationData":[TD([[makeQuery(id+"F1.imprint","IMPRINT",EDGE,{"disambiguationData":[TD([[subQ8,1.0]])],"derivedFrom":subQ1}),-1.0]])]});}
            var Q39;
            {var subQ1=sQuery(id+"F1.wireOp",EDGE,"E4.3.0.9");var subQ7=sQuery(id+"F1.wireOp",EDGE,"E4.3.0.5");var subQ8=makeQuery(id+"F1.imprint","INTERSECT",VERTEX,{"derivedFrom":[subQ7,subQ1]});Q39=makeQuery(id+"F1.imprint","IMPRINT",FACE,{"disambiguationData":[TD([[makeQuery(id+"F1.imprint","IMPRINT",EDGE,{"disambiguationData":[TD([[subQ8,1.0]])],"derivedFrom":subQ1}),-1.0]])]});}
            var Q40;
            {var subQ5=sQuery(id+"F1.wireOp",EDGE,"E3.1.0.12");var subQ7=sQuery(id+"F1.wireOp",EDGE,"E3.1.0.6");var subQ8=makeQuery(id+"F1.imprint","INTERSECT",VERTEX,{"derivedFrom":[subQ7,subQ5]});Q40=makeQuery(id+"F1.imprint","IMPRINT",FACE,{"disambiguationData":[TD([[makeQuery(id+"F1.imprint","IMPRINT",EDGE,{"disambiguationData":[TD([[subQ8,-1.0]])],"derivedFrom":subQ5}),-1.0]])]});}
            var Q41;
            {var subQ1=sQuery(id+"F1.wireOp",EDGE,"E2.1.0.8");var subQ5=sQuery(id+"F1.wireOp",EDGE,"E2.1.0.7");var subQ6=makeQuery(id+"F1.imprint","INTERSECT",VERTEX,{"derivedFrom":[subQ5,subQ1]});Q41=makeQuery(id+"F1.imprint","IMPRINT",FACE,{"disambiguationData":[TD([[makeQuery(id+"F1.imprint","IMPRINT",EDGE,{"disambiguationData":[TD([[subQ6,1.0]])],"derivedFrom":subQ1}),-1.0]])]});}
            var Q42;
            {var subQ5=sQuery(id+"F1.wireOp",EDGE,"E4.1.0.7");var subQ7=sQuery(id+"F1.wireOp",EDGE,"E4.1.0.4");var subQ8=makeQuery(id+"F1.imprint","INTERSECT",VERTEX,{"derivedFrom":[subQ7,subQ5]});Q42=makeQuery(id+"F1.imprint","IMPRINT",FACE,{"disambiguationData":[TD([[makeQuery(id+"F1.imprint","IMPRINT",EDGE,{"disambiguationData":[TD([[subQ8,-1.0]])],"derivedFrom":subQ5}),-1.0]])]});}
            var Q43;
            {var subQ5=sQuery(id+"F1.wireOp",EDGE,"E2.2.0.8");var subQ7=sQuery(id+"F1.wireOp",EDGE,"E2.2.0.7");var subQ8=makeQuery(id+"F1.imprint","INTERSECT",VERTEX,{"derivedFrom":[subQ7,subQ5]});Q43=makeQuery(id+"F1.imprint","IMPRINT",FACE,{"disambiguationData":[TD([[makeQuery(id+"F1.imprint","IMPRINT",EDGE,{"disambiguationData":[TD([[subQ8,1.0]])],"derivedFrom":subQ5}),-1.0]])]});}
            var Q44;
            {var subQ5=sQuery(id+"F1.wireOp",EDGE,"E4.2.0.7");var subQ7=sQuery(id+"F1.wireOp",EDGE,"E4.2.0.4");var subQ8=makeQuery(id+"F1.imprint","INTERSECT",VERTEX,{"derivedFrom":[subQ7,subQ5]});Q44=makeQuery(id+"F1.imprint","IMPRINT",FACE,{"disambiguationData":[TD([[makeQuery(id+"F1.imprint","IMPRINT",EDGE,{"disambiguationData":[TD([[subQ8,-1.0]])],"derivedFrom":subQ5}),-1.0]])]});}
            var Q45;
            {var subQ5=sQuery(id+"F1.wireOp",EDGE,"E4.1.0.9");var subQ7=sQuery(id+"F1.wireOp",EDGE,"E4.1.0.5");var subQ8=makeQuery(id+"F1.imprint","INTERSECT",VERTEX,{"derivedFrom":[subQ7,subQ5]});Q45=makeQuery(id+"F1.imprint","IMPRINT",FACE,{"disambiguationData":[TD([[makeQuery(id+"F1.imprint","IMPRINT",EDGE,{"disambiguationData":[TD([[subQ8,1.0]])],"derivedFrom":subQ5}),-1.0]])]});}
            var Q46;
            {var subQ1=sQuery(id+"F1.wireOp",EDGE,"E4.2.0.9");var subQ7=sQuery(id+"F1.wireOp",EDGE,"E4.2.0.5");var subQ8=makeQuery(id+"F1.imprint","INTERSECT",VERTEX,{"derivedFrom":[subQ7,subQ1]});Q46=makeQuery(id+"F1.imprint","IMPRINT",FACE,{"disambiguationData":[TD([[makeQuery(id+"F1.imprint","IMPRINT",EDGE,{"disambiguationData":[TD([[subQ8,1.0]])],"derivedFrom":subQ1}),-1.0]])]});}
            extrude(context, id + "F4", {"entities" : qUnion([Q0, Q1, Q2, Q3, Q4, Q5, Q6, Q7, Q8, Q9, Q10, Q11, Q12, Q13, Q14, Q15, Q16, Q17, Q18, Q19, Q20, Q21, Q22, Q23, Q24, Q25, Q26, Q27, Q28, Q29, Q30, Q31, Q32, Q33, Q34, Q35, Q36, Q37, Q38, Q39, Q40, Q41, Q42, Q43, Q44, Q45, Q46]), "operationType" : NewBodyOperationType.ADD, "depth" : (getVariable(context, 'WallThickness')) * mm});
        }
    });
